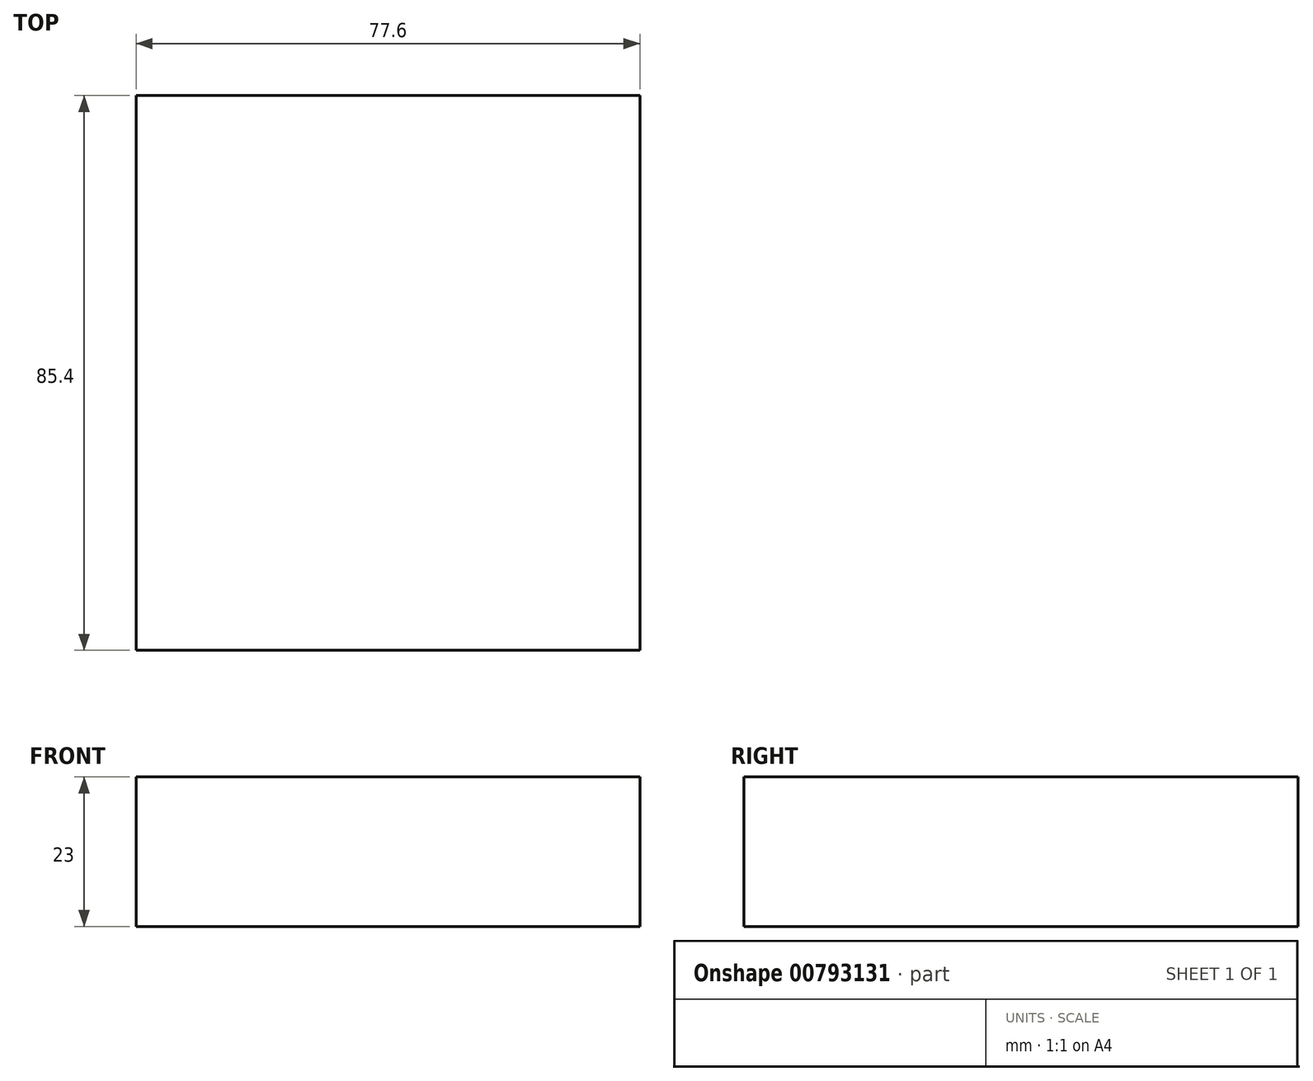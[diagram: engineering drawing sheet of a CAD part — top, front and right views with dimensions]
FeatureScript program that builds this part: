
annotation { "Feature Type Name" : "Feature", "Feature Type Description" : "" }
export const myFeature = defineFeature(function(context is Context, id is Id, definition is map)
    precondition{}
    {
        {
            var Q0;
            Q0=qCreatedBy(makeId("Top.planeOp"),FACE);
            var sketch = newSketch(context, id + "F0", { "sketchPlane" : qUnion([Q0])});
            skLineSegment(sketch, "E0.bottom", {"start": v(-70.96, 0) * mm, "end": v(6.64, 0) * mm});
            skLineSegment(sketch, "E0.top", {"start": v(-70.96, 85.4) * mm, "end": v(6.64, 85.4) * mm});
            skLineSegment(sketch, "E0.left", {"start": v(-70.96, 0) * mm, "end": v(-70.96, 85.4) * mm});
            skLineSegment(sketch, "E0.right", {"start": v(6.64, 0) * mm, "end": v(6.64, 85.4) * mm});
            skSolve(sketch);
        }
        {
            var Q0;
            Q0=qSketchRegion(id+"F0",true);
            extrude(context, id + "F1", {"entities" : qUnion([Q0]), "depth" : 23 * mm, "offsetDistance" : 25.4 * mm});
        }
    });
